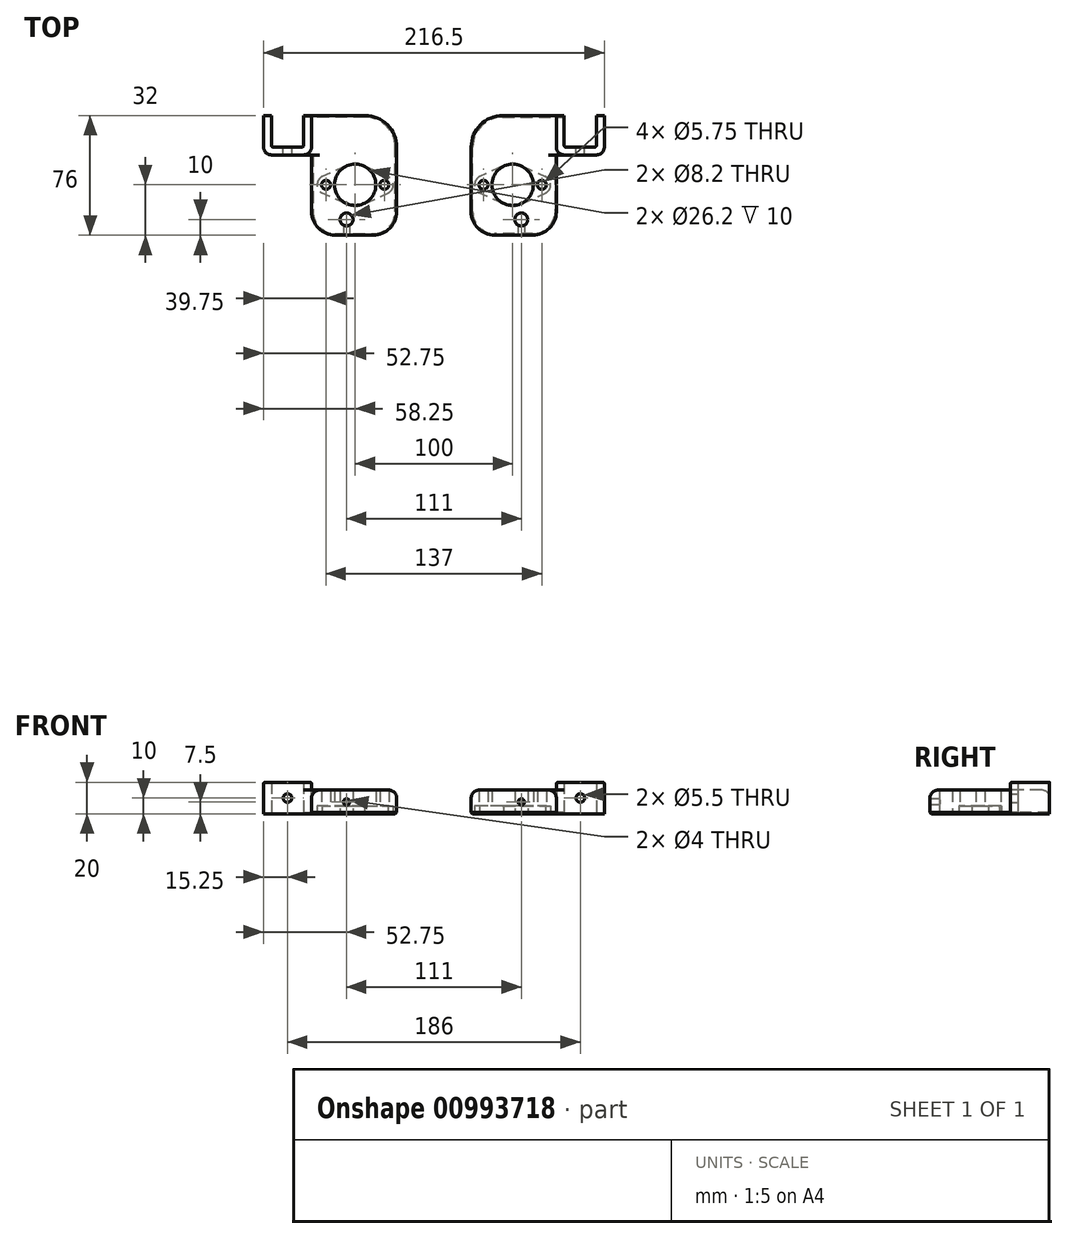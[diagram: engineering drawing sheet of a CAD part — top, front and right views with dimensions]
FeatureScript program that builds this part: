
annotation { "Feature Type Name" : "Feature", "Feature Type Description" : "" }
export const myFeature = defineFeature(function(context is Context, id is Id, definition is map)
    precondition{}
    {
        {
            var Q0;
            Q0=qCreatedBy(makeId("Top.planeOp"),FACE);
            var sketch = newSketch(context, id + "F0", { "sketchPlane" : qUnion([Q0])});
            skArc(sketch, "E0", {"start": v(10.42, -7.94) * mm, "mid": v(0, 13.1) * mm, "end": v(-10.42, -7.94) * mm});
            skCircle(sketch, "E1", {"center": v(-18.5, 0) * mm, "radius": 2.88 * mm});
            skCircle(sketch, "E2", {"center": v(18.5, 0) * mm, "radius": 2.88 * mm});
            skLineSegment(sketch, "E3.bottom", {"start": v(32.75, 44) * mm, "end": v(53.25, 44) * mm});
            skLineSegment(sketch, "E3.top", {"start": v(32.75, 24) * mm, "end": v(53.25, 24) * mm});
            skLineSegment(sketch, "E3.left", {"start": v(32.75, 44) * mm, "end": v(32.75, 24) * mm});
            skLineSegment(sketch, "E3.right", {"start": v(53.25, 44) * mm, "end": v(53.25, 24) * mm});
            skLineSegment(sketch, "E4.bottom", {"start": v(-6.38, 44) * mm, "end": v(58.25, 44) * mm});
            skLineSegment(sketch, "E4.right", {"start": v(58.25, 44) * mm, "end": v(58.25, 24) * mm});
            skLineSegment(sketch, "E5", {"start": v(43, 24) * mm, "end": v(43, 44) * mm, "construction": true});
            skLineSegment(sketch, "E6.top", {"start": v(53.25, 19) * mm, "end": v(43, 19) * mm});
            skPoint(sketch, "E7.visualSharp", {"position": v(-23, 44) * mm});
            skArc(sketch, "E7.filletArc", {"start": v(-6.38, 44) * mm, "mid": v(-20.52, 38.14) * mm, "end": v(-26.38, 24) * mm});
            skPoint(sketch, "E8.visualSharp", {"position": v(23, 19) * mm});
            skPoint(sketch, "E9.visualSharp", {"position": v(58.25, 19) * mm});
            skArc(sketch, "E9.filletArc", {"start": v(53.25, 19) * mm, "mid": v(56.79, 20.46) * mm, "end": v(58.25, 24) * mm});
            skLineSegment(sketch, "E10", {"start": v(27.75, 44) * mm, "end": v(27.75, 11.94) * mm});
            skCircle(sketch, "E11", {"center": v(5.5, -22) * mm, "radius": 4.1 * mm});
            skLineSegment(sketch, "E12", {"start": v(-26.38, 24) * mm, "end": v(-26.38, -17) * mm});
            skLineSegment(sketch, "E13", {"start": v(-11.37, -32) * mm, "end": v(12.75, -32) * mm});
            skLineSegment(sketch, "E14", {"start": v(27.75, -17) * mm, "end": v(27.75, 11.94) * mm});
            skLineSegment(sketch, "E15", {"start": v(43, 19) * mm, "end": v(27.75, 19) * mm});
            skCircle(sketch, "E16", {"center": v(0, 0) * mm, "radius": 13.1 * mm});
            skPoint(sketch, "E17.visualSharp", {"position": v(-26.37, -32) * mm});
            skArc(sketch, "E17.filletArc", {"start": v(-26.37, -17) * mm, "mid": v(-21.98, -27.6) * mm, "end": v(-11.37, -32) * mm});
            skPoint(sketch, "E18.visualSharp", {"position": v(27.75, -32) * mm});
            skArc(sketch, "E18.filletArc", {"start": v(12.75, -32) * mm, "mid": v(23.36, -27.6) * mm, "end": v(27.75, -17) * mm});
            skSolve(sketch);
        }
        {
            var Q0;
            Q0=makeQuery(id+"F0.imprint","IMPRINT",FACE,{"disambiguationData":[TD([[makeQuery(id+"F0.imprint","IMPRINT",EDGE,{"derivedFrom":sQuery(id+"F0.wireOp",EDGE,"E0")}),-1.0]])]});
            var Q1;
            Q1=makeQuery(id+"F0.imprint","IMPRINT",FACE,{"disambiguationData":[TD([[makeQuery(id+"F0.imprint","IMPRINT",EDGE,{"derivedFrom":sQuery(id+"F0.wireOp",EDGE,"E1")}),-1.0]])]});
            extrude(context, id + "F1", {"entities" : qUnion([Q0, Q1]), "depth" : 15 * mm, "offsetDistance" : 25 * mm});
        }
        {
            var Q0;
            Q0=makeQuery(id+"F0.imprint","IMPRINT",FACE,{"disambiguationData":[TD([[makeQuery(id+"F0.imprint","IMPRINT",EDGE,{"derivedFrom":sQuery(id+"F0.wireOp",EDGE,"E3.top")}),-1.0]])]});
            extrude(context, id + "F2", {"entities" : qUnion([Q0]), "operationType" : NewBodyOperationType.ADD, "depth" : 20 * mm, "offsetDistance" : 25 * mm});
        }
        {
            var Q0;
            Q0=makeQuery(id+"F2.opExtrude","SWEPT_FACE",FACE,{"disambiguationData":[OSD([sQuery(id+"F0.wireOp",EDGE,"E3.top")])]});
            var sketch = newSketch(context, id + "F3", { "sketchPlane" : qUnion([Q0])});
            skCircle(sketch, "E19", {"center": v(-43, 10) * mm, "radius": 2.75 * mm});
            skPoint(sketch, "E19.centerSnap0", {"position": v(-43, 20) * mm});
            skSolve(sketch);
        }
        {
            var Q0;
            Q0=makeQuery(id+"F3.imprint","IMPRINT",FACE,{"disambiguationData":[TD([[makeQuery(id+"F3.imprint","IMPRINT",EDGE,{"derivedFrom":sQuery(id+"F3.wireOp",EDGE,"E19")}),1.0]])]});
            extrude(context, id + "F4", {"entities" : qUnion([Q0]), "operationType" : NewBodyOperationType.REMOVE, "oppositeDirection" : true, "depth" : 25 * mm, "offsetDistance" : 25 * mm});
        }
        {
            var Q0;
            Q0=makeQuery(id+"F1.opExtrude","SWEPT_FACE",FACE,{"disambiguationData":[OSD([sQuery(id+"F0.wireOp",EDGE,"E13")])]});
            var sketch = newSketch(context, id + "F5", { "sketchPlane" : qUnion([Q0])});
            skLineSegment(sketch, "E20.0", {"start": v(1.4, 0) * mm, "end": v(9.6, 0) * mm});
            skCircle(sketch, "E21", {"center": v(5.5, 7.5) * mm, "radius": 2 * mm});
            skPoint(sketch, "E21.centerSnap0", {"position": v(5.5, 0) * mm});
            skSolve(sketch);
        }
        {
            var Q0;
            Q0=makeQuery(id+"F5.imprint","IMPRINT",FACE,{"disambiguationData":[TD([[makeQuery(id+"F5.imprint","IMPRINT",EDGE,{"derivedFrom":sQuery(id+"F5.wireOp",EDGE,"E21")}),1.0]])]});
            extrude(context, id + "F6", {"entities" : qUnion([Q0]), "operationType" : NewBodyOperationType.REMOVE, "oppositeDirection" : true, "depth" : 6.5 * mm, "offsetDistance" : 25 * mm});
        }
        {
            var Q0;
            {var subQ0=sQuery(id+"F0.wireOp",EDGE,"E14");var subQ1=sQuery(id+"F0.wireOp",EDGE,"E10");Q0=makeQuery(id+"F2.boolean.opBoolean","SPLIT",EDGE,{"disambiguationData":[topologyDisambiguationEdgeConnected([makeQuery(id+"F2.opExtrude","SWEPT_FACE",FACE,{"disambiguationData":[OSD([subQ1])]})])],"derivedFrom":makeQuery(id+"F1.opExtrude","CAP_EDGE",EDGE,{"disambiguationData":[OSD([subQ1,subQ0])],"isStart":false})});}
            fillet(context, id + "F7", {"entities" : qUnion([Q0]), "radius" : 5 * mm, "tangentPropagation" : true, "allowEdgeOverflow" : false});
        }
        {
            var Q0;
            {var subQ0=sQuery(id+"F0.wireOp",EDGE,"E14");var subQ1=sQuery(id+"F0.wireOp",EDGE,"E10");Q0=makeQuery(id+"F2.boolean.opBoolean","SPLIT",EDGE,{"disambiguationData":[topologyDisambiguationEdgeConnected([makeQuery(id+"F1.opExtrude","SWEPT_FACE",FACE,{"disambiguationData":[OSD([subQ1,subQ0])]})])],"derivedFrom":makeQuery(id+"F1.opExtrude","CAP_EDGE",EDGE,{"disambiguationData":[OSD([subQ1,subQ0])],"isStart":false})});}
            var Q1;
            Q1=makeQuery(id+"F2.opExtrude","CAP_EDGE",EDGE,{"disambiguationData":[OSD([sQuery(id+"F0.wireOp",EDGE,"E6.top"),sQuery(id+"F0.wireOp",EDGE,"E15")])],"isStart":false});
            var Q2;
            Q2=makeQuery(id+"F2.opExtrude","CAP_EDGE",EDGE,{"disambiguationData":[OSD([sQuery(id+"F0.wireOp",EDGE,"E10")])],"isStart":false});
            var Q3;
            Q3=makeQuery(id+"F2.opExtrude","SWEPT_EDGE",EDGE,{"disambiguationData":[OSD([sQuery(id+"F0.wireOp",EDGE,"E3.top"),sQuery(id+"F0.wireOp",EDGE,"E3.left")])]});
            var Q4;
            Q4=makeQuery(id+"F2.opExtrude","SWEPT_EDGE",EDGE,{"disambiguationData":[OSD([sQuery(id+"F0.wireOp",EDGE,"E3.top"),sQuery(id+"F0.wireOp",EDGE,"E3.right")])]});
            fillet(context, id + "F8", {"entities" : qUnion([Q0, Q1, Q2, Q3, Q4]), "radius" : 1 * mm, "tangentPropagation" : true, "allowEdgeOverflow" : false});
        }
        {
            var Q0;
            {var subQ0=sQuery(id+"F0.wireOp",EDGE,"E10");var subQ1=sQuery(id+"F0.wireOp",EDGE,"E15");Q0=makeQuery(id+"F2.boolean.opBoolean","SPLIT",EDGE,{"disambiguationData":[topologyDisambiguationEdgeConnected([makeQuery(id+"F1.opExtrude","SWEPT_FACE",FACE,{"disambiguationData":[OSD([subQ0,sQuery(id+"F0.wireOp",EDGE,"E14")])]})])],"derivedFrom":makeQuery(id+"F2.opExtrude","SWEPT_EDGE",EDGE,{"disambiguationData":[OSD([subQ0,subQ1])]})});}
            fillet(context, id + "F9", {"entities" : qUnion([Q0]), "radius" : 5 * mm, "tangentPropagation" : true, "allowEdgeOverflow" : false});
        }
        {
            var Q0;
            Q0=makeQuery(id+"F1.opExtrude","CAP_EDGE",EDGE,{"disambiguationData":[OSD([sQuery(id+"F0.wireOp",EDGE,"E7.filletArc")])],"isStart":true});
            chamfer(context, id + "F10", {"entities" : qUnion([Q0]), "width" : 1 * mm, "tangentPropagation" : true});
        }
        {
            var Q0;
            Q0=qCreatedBy(makeId("Right.planeOp"),FACE);
            cPlane(context, id + "F11", {"entities" : qUnion([Q0]), "cplaneType" : CPlaneType.OFFSET, "offset" : 50 * mm, "oppositeDirection" : true, "width" : 150 * mm, "height" : 150 * mm});
        }
        {
            var Q0;
            Q0=makeQuery(id+"F0.imprint","IMPRINT",FACE,{"disambiguationData":[TD([[makeQuery(id+"F0.imprint","IMPRINT",EDGE,{"derivedFrom":sQuery(id+"F0.wireOp",EDGE,"E1")}),-1.0]])]});
            var sketch = newSketch(context, id + "F12", { "sketchPlane" : qUnion([Q0])});
            skLineSegment(sketch, "E22", {"start": v(6.57, 11.84) * mm, "end": v(20.93, 5.26) * mm});
            skLineSegment(sketch, "E23", {"start": v(5.63, -12.27) * mm, "end": v(20.93, -5.26) * mm});
            skArc(sketch, "E24.trimOffspring", {"start": v(-6.55, -11.8) * mm, "mid": v(-0.52, -13.5) * mm, "end": v(5.63, -12.27) * mm});
            skPoint(sketch, "E25.center.orphan", {"position": v(-18.5, 0) * mm});
            skArc(sketch, "E26.trimOffspring", {"start": v(20.93, -5.26) * mm, "mid": v(24.17, 0) * mm, "end": v(20.93, 5.26) * mm});
            skArc(sketch, "E27.trimOffspring", {"start": v(13.5, -0.18) * mm, "mid": v(13.5, 0) * mm, "end": v(13.5, 0.18) * mm});
            skArc(sketch, "E28.trimOffspring", {"start": v(5.63, 12.27) * mm, "mid": v(-0.14, 13.5) * mm, "end": v(-5.89, 12.15) * mm});
            skLineSegment(sketch, "E29.MirrorCS", {"start": v(-6.57, 11.84) * mm, "end": v(-20.93, 5.26) * mm});
            skLineSegment(sketch, "E30.MirrorCS", {"start": v(-5.63, -12.27) * mm, "end": v(-20.93, -5.26) * mm});
            skArc(sketch, "E31.MirrorCS", {"start": v(-20.93, -5.26) * mm, "mid": v(-24.17, 0) * mm, "end": v(-20.93, 5.26) * mm});
            skLineSegment(sketch, "E32", {"start": v(-6.57, 11.84) * mm, "end": v(-5.89, 12.15) * mm});
            skLineSegment(sketch, "E33", {"start": v(5.63, 12.27) * mm, "end": v(6.57, 11.84) * mm});
            skSolve(sketch);
        }
        {
            var Q0;
            Q0=makeQuery(id+"F12.imprint","IMPRINT",FACE,{"disambiguationData":[TD([[makeQuery(id+"F12.imprint","IMPRINT",EDGE,{"derivedFrom":sQuery(id+"F12.wireOp",EDGE,"E23")}),1.0]])]});
            extrude(context, id + "F13", {"entities" : qUnion([Q0]), "operationType" : NewBodyOperationType.REMOVE, "depth" : 5 * mm, "offsetDistance" : 25 * mm});
        }
        {
            var Q0;
            Q0=makeQuery(id+"F1.opExtrude","SWEPT_BODY",BODY,{"disambiguationData":[OSD([sQuery(id+"F0.wireOp",EDGE,"E1"),sQuery(id+"F0.wireOp",EDGE,"E2"),sQuery(id+"F0.wireOp",EDGE,"E4.bottom"),sQuery(id+"F0.wireOp",EDGE,"E7.filletArc"),sQuery(id+"F0.wireOp",EDGE,"E10"),sQuery(id+"F0.wireOp",EDGE,"E11"),sQuery(id+"F0.wireOp",EDGE,"E12"),sQuery(id+"F0.wireOp",EDGE,"E13"),sQuery(id+"F0.wireOp",EDGE,"E14"),sQuery(id+"F0.wireOp",EDGE,"E16"),sQuery(id+"F0.wireOp",EDGE,"E17.filletArc"),sQuery(id+"F0.wireOp",EDGE,"E18.filletArc")])]});
            var Q1;
            Q1=qCreatedBy(id+"F11.planeOp",FACE);
            mirror(context, id + "F14", {"operationType" : NewBodyOperationType.ADD, "entities" : qUnion([Q0]), "mirrorPlane" : qUnion([Q1])});
        }
    });
